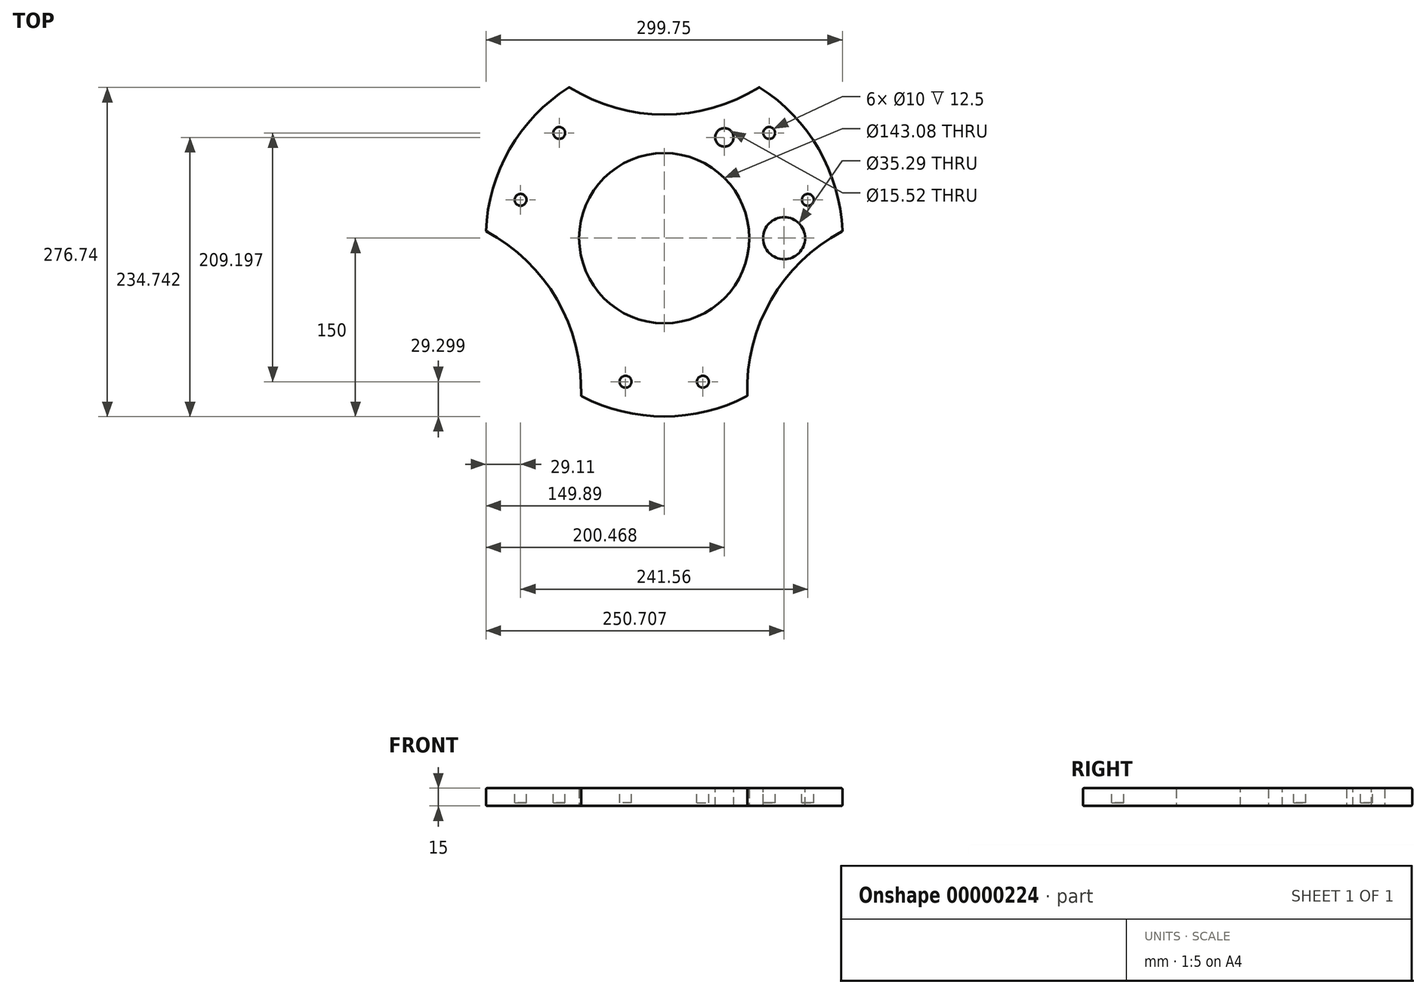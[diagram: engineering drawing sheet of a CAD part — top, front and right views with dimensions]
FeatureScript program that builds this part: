
annotation { "Feature Type Name" : "Feature", "Feature Type Description" : "" }
export const myFeature = defineFeature(function(context is Context, id is Id, definition is map)
    precondition{}
    {
        {
            var Q0;
            Q0 = qCreatedBy(makeId("Top.planeOp"), FACE);
            var sketch = newSketch(context, id + "F0", { "sketchPlane" : qUnion([Q0])});
            skLineSegment(sketch, "E0", {"start": v(0, 0) * mm, "end": v(0, -150) * mm, "construction": true});
            skArc(sketch, "E1", {"start": v(-61.95, 35.77) * mm, "mid": v(-61.95, -35.77) * mm, "end": v(0, -71.54) * mm});
            skArc(sketch, "E2", {"start": v(-129.9, 75) * mm, "mid": v(-144.12, 41.6) * mm, "end": v(-149.89, 5.76) * mm});
            skLineSegment(sketch, "E3", {"start": v(0, 0) * mm, "end": v(-129.9, -75) * mm, "construction": true});
            skArc(sketch, "E4", {"start": v(-69.95, -132.69) * mm, "mid": v(-89.94, -51.93) * mm, "end": v(-149.89, 5.76) * mm});
            skLineSegment(sketch, "E5", {"start": v(0, 0) * mm, "end": v(-129.9, 75) * mm, "construction": true});
            skLineSegment(sketch, "E6", {"start": v(-129.9, 75) * mm, "end": v(-61.95, 35.77) * mm});
            skLineSegment(sketch, "E7", {"start": v(0, -71.54) * mm, "end": v(0, -150) * mm});
            skArc(sketch, "E8.trimOffspring", {"start": v(-69.95, -132.69) * mm, "mid": v(-36.03, -145.6) * mm, "end": v(0, -150) * mm});
            skSolve(sketch);
        }
        {
            var Q0;
            Q0=makeQuery(id+"F0.imprint","IMPRINT",FACE,{"disambiguationData":[TD([[makeQuery(id+"F0.imprint","IMPRINT",EDGE,{"derivedFrom":sQuery(id+"F0.wireOp",EDGE,"E1")}),-1.0]])]});
            extrude(context, id + "F1", {"entities" : qUnion([Q0]), "depth" : 15 * mm});
        }
        {
            var Q0;
            Q0=makeQuery(id+"F1.opExtrude","CAP_FACE",FACE,{"disambiguationData":[OSD([sQuery(id+"F0.wireOp",EDGE,"E1"),sQuery(id+"F0.wireOp",EDGE,"E2"),sQuery(id+"F0.wireOp",EDGE,"E4"),sQuery(id+"F0.wireOp",EDGE,"E6"),sQuery(id+"F0.wireOp",EDGE,"E7"),sQuery(id+"F0.wireOp",EDGE,"E8.trimOffspring")])],"isStart":false});
            var sketch = newSketch(context, id + "F2", { "sketchPlane" : qUnion([Q0])});
            skCircle(sketch, "E9", {"center": v(-32.5, -120.7) * mm, "radius": 5 * mm});
            skCircle(sketch, "E10", {"center": v(0, 0) * mm, "radius": 125 * mm, "construction": true});
            skLineSegment(sketch, "E11.0", {"start": v(0, 0) * mm, "end": v(-129.9, -75) * mm, "construction": true});
            skLineSegment(sketch, "E12.0", {"start": v(0, 0) * mm, "end": v(0, -150) * mm, "construction": true});
            skSolve(sketch);
        }
        {
            var Q0;
            Q0=makeQuery(id+"F2.imprint","IMPRINT",FACE,{"disambiguationData":[TD([[makeQuery(id+"F2.imprint","IMPRINT",EDGE,{"derivedFrom":sQuery(id+"F2.wireOp",EDGE,"E9")}),1.0]])]});
            extrude(context, id + "F3", {"entities" : qUnion([Q0]), "oppositeDirection" : true, "depth" : 12.5 * mm});
        }
        {
            var Q0;
            Q0=sQuery(id+"F0.wireOp",EDGE,"E3");
            cPlane(context, id + "F4", {"entities" : qUnion([Q0]), "cplaneType" : CPlaneType.LINE_ANGLE, "offset" : 150 * mm, "angle" : 0 * degree, "width" : 150 * mm, "height" : 150 * mm});
        }
        {
            var Q0;
            Q0=makeQuery(id+"F3.opExtrude","SWEPT_BODY",BODY,{"disambiguationData":[OSD([sQuery(id+"F2.wireOp",EDGE,"E9")])]});
            var Q1;
            Q1=qCreatedBy(id+"F4.planeOp",FACE);
            mirror(context, id + "F5", {"entities" : qUnion([Q0]), "mirrorPlane" : qUnion([Q1])});
        }
        {
            var Q0;
            Q0=makeQuery(id+"F3.opExtrude","SWEPT_BODY",BODY,{"disambiguationData":[OSD([sQuery(id+"F2.wireOp",EDGE,"E9")])]});
            var Q1;
            Q1=makeQuery(id+"F5.opPattern","COPY",BODY,{"derivedFrom":makeQuery(id+"F3.opExtrude","SWEPT_BODY",BODY,{"disambiguationData":[OSD([sQuery(id+"F2.wireOp",EDGE,"E9")])]}),"instanceName":"1"});
            var Q2;
            Q2=makeQuery(id+"F1.opExtrude","SWEPT_BODY",BODY,{"disambiguationData":[OSD([sQuery(id+"F0.wireOp",EDGE,"E1"),sQuery(id+"F0.wireOp",EDGE,"E2"),sQuery(id+"F0.wireOp",EDGE,"E4"),sQuery(id+"F0.wireOp",EDGE,"E6"),sQuery(id+"F0.wireOp",EDGE,"E7"),sQuery(id+"F0.wireOp",EDGE,"E8.trimOffspring")])]});
            booleanBodies(context, id + "F6", {"operationType" : BooleanOperationType.SUBTRACTION, "tools" : qUnion([Q0, Q1]), "targets" : qUnion([Q2])});
        }
        {
            var Q0;
            Q0=makeQuery(id+"F1.opExtrude","SWEPT_BODY",BODY,{"disambiguationData":[OSD([sQuery(id+"F0.wireOp",EDGE,"E1"),sQuery(id+"F0.wireOp",EDGE,"E2"),sQuery(id+"F0.wireOp",EDGE,"E4"),sQuery(id+"F0.wireOp",EDGE,"E6"),sQuery(id+"F0.wireOp",EDGE,"E7"),sQuery(id+"F0.wireOp",EDGE,"E8.trimOffspring")])]});
            var Q1;
            Q1=makeQuery(id+"F1.opExtrude","SWEPT_FACE",FACE,{"disambiguationData":[OSD([sQuery(id+"F0.wireOp",EDGE,"E1")])]});
            circularPattern(context, id + "F7", {"entities" : qUnion([Q0]), "axis" : qUnion([Q1]), "angle" : 360 * degree, "instanceCount" : 3, "equalSpace" : true});
        }
        {
            var Q0;
            Q0=makeQuery(id+"F1.opExtrude","SWEPT_BODY",BODY,{"disambiguationData":[OSD([sQuery(id+"F0.wireOp",EDGE,"E1"),sQuery(id+"F0.wireOp",EDGE,"E2"),sQuery(id+"F0.wireOp",EDGE,"E4"),sQuery(id+"F0.wireOp",EDGE,"E6"),sQuery(id+"F0.wireOp",EDGE,"E7"),sQuery(id+"F0.wireOp",EDGE,"E8.trimOffspring")])]});
            var Q1;
            Q1=makeQuery(id+"F7.opPattern","COPY",BODY,{"derivedFrom":makeQuery(id+"F1.opExtrude","SWEPT_BODY",BODY,{"disambiguationData":[OSD([sQuery(id+"F0.wireOp",EDGE,"E1"),sQuery(id+"F0.wireOp",EDGE,"E2"),sQuery(id+"F0.wireOp",EDGE,"E4"),sQuery(id+"F0.wireOp",EDGE,"E6"),sQuery(id+"F0.wireOp",EDGE,"E7"),sQuery(id+"F0.wireOp",EDGE,"E8.trimOffspring")])]}),"instanceName":"2"});
            var Q2;
            Q2=makeQuery(id+"F7.opPattern","COPY",BODY,{"derivedFrom":makeQuery(id+"F1.opExtrude","SWEPT_BODY",BODY,{"disambiguationData":[OSD([sQuery(id+"F0.wireOp",EDGE,"E1"),sQuery(id+"F0.wireOp",EDGE,"E2"),sQuery(id+"F0.wireOp",EDGE,"E4"),sQuery(id+"F0.wireOp",EDGE,"E6"),sQuery(id+"F0.wireOp",EDGE,"E7"),sQuery(id+"F0.wireOp",EDGE,"E8.trimOffspring")])]}),"instanceName":"1"});
            booleanBodies(context, id + "F8", {"operationType" : BooleanOperationType.UNION, "tools" : qUnion([Q0, Q1, Q2])});
        }
        {
            var Q0;
            Q0=makeQuery(id+"F8.opBoolean","MERGE",EDGE,{"derivedFrom":[makeQuery(id+"F1.opExtrude","CAP_EDGE",EDGE,{"disambiguationData":[OSD([sQuery(id+"F0.wireOp",EDGE,"E8.trimOffspring")])],"isStart":false}),makeQuery(id+"F7.opPattern","COPY",EDGE,{"derivedFrom":makeQuery(id+"F1.opExtrude","CAP_EDGE",EDGE,{"disambiguationData":[OSD([sQuery(id+"F0.wireOp",EDGE,"E2")])],"isStart":false}),"instanceName":"1"})]});
            var Q1;
            Q1=makeQuery(id+"F7.opPattern","COPY",EDGE,{"derivedFrom":makeQuery(id+"F1.opExtrude","SWEPT_EDGE",EDGE,{"disambiguationData":[OSD([sQuery(id+"F0.wireOp",EDGE,"E2"),sQuery(id+"F0.wireOp",EDGE,"E4")])]}),"instanceName":"1"});
            var Q2;
            Q2=makeQuery(id+"F7.opPattern","COPY",EDGE,{"derivedFrom":makeQuery(id+"F1.opExtrude","CAP_EDGE",EDGE,{"disambiguationData":[OSD([sQuery(id+"F0.wireOp",EDGE,"E4")])],"isStart":false}),"instanceName":"1"});
            var Q3;
            Q3=makeQuery(id+"F7.opPattern","COPY",EDGE,{"derivedFrom":makeQuery(id+"F1.opExtrude","SWEPT_EDGE",EDGE,{"disambiguationData":[OSD([sQuery(id+"F0.wireOp",EDGE,"E4"),sQuery(id+"F0.wireOp",EDGE,"E8.trimOffspring")])]}),"instanceName":"1"});
            var Q4;
            Q4=makeQuery(id+"F8.opBoolean","MERGE",EDGE,{"derivedFrom":[makeQuery(id+"F7.opPattern","COPY",EDGE,{"derivedFrom":makeQuery(id+"F1.opExtrude","CAP_EDGE",EDGE,{"disambiguationData":[OSD([sQuery(id+"F0.wireOp",EDGE,"E8.trimOffspring")])],"isStart":false}),"instanceName":"1"}),makeQuery(id+"F7.opPattern","COPY",EDGE,{"derivedFrom":makeQuery(id+"F1.opExtrude","CAP_EDGE",EDGE,{"disambiguationData":[OSD([sQuery(id+"F0.wireOp",EDGE,"E2")])],"isStart":false}),"instanceName":"2"})]});
            var Q5;
            Q5=makeQuery(id+"F7.opPattern","COPY",EDGE,{"derivedFrom":makeQuery(id+"F1.opExtrude","SWEPT_EDGE",EDGE,{"disambiguationData":[OSD([sQuery(id+"F0.wireOp",EDGE,"E2"),sQuery(id+"F0.wireOp",EDGE,"E4")])]}),"instanceName":"2"});
            var Q6;
            Q6=makeQuery(id+"F7.opPattern","COPY",EDGE,{"derivedFrom":makeQuery(id+"F1.opExtrude","CAP_EDGE",EDGE,{"disambiguationData":[OSD([sQuery(id+"F0.wireOp",EDGE,"E4")])],"isStart":false}),"instanceName":"2"});
            var Q7;
            Q7=makeQuery(id+"F7.opPattern","COPY",EDGE,{"derivedFrom":makeQuery(id+"F1.opExtrude","SWEPT_EDGE",EDGE,{"disambiguationData":[OSD([sQuery(id+"F0.wireOp",EDGE,"E4"),sQuery(id+"F0.wireOp",EDGE,"E8.trimOffspring")])]}),"instanceName":"2"});
            var Q8;
            Q8=makeQuery(id+"F8.opBoolean","MERGE",EDGE,{"derivedFrom":[makeQuery(id+"F1.opExtrude","CAP_EDGE",EDGE,{"disambiguationData":[OSD([sQuery(id+"F0.wireOp",EDGE,"E2")])],"isStart":false}),makeQuery(id+"F7.opPattern","COPY",EDGE,{"derivedFrom":makeQuery(id+"F1.opExtrude","CAP_EDGE",EDGE,{"disambiguationData":[OSD([sQuery(id+"F0.wireOp",EDGE,"E8.trimOffspring")])],"isStart":false}),"instanceName":"2"})]});
            var Q9;
            Q9=makeQuery(id+"F1.opExtrude","CAP_EDGE",EDGE,{"disambiguationData":[OSD([sQuery(id+"F0.wireOp",EDGE,"E4")])],"isStart":false});
            var Q10;
            Q10=makeQuery(id+"F1.opExtrude","SWEPT_EDGE",EDGE,{"disambiguationData":[OSD([sQuery(id+"F0.wireOp",EDGE,"E4"),sQuery(id+"F0.wireOp",EDGE,"E8.trimOffspring")])]});
            var Q11;
            Q11=makeQuery(id+"F8.opBoolean","MERGE",EDGE,{"derivedFrom":[makeQuery(id+"F1.opExtrude","CAP_EDGE",EDGE,{"disambiguationData":[OSD([sQuery(id+"F0.wireOp",EDGE,"E8.trimOffspring")])],"isStart":true}),makeQuery(id+"F7.opPattern","COPY",EDGE,{"derivedFrom":makeQuery(id+"F1.opExtrude","CAP_EDGE",EDGE,{"disambiguationData":[OSD([sQuery(id+"F0.wireOp",EDGE,"E2")])],"isStart":true}),"instanceName":"1"})]});
            var Q12;
            Q12=makeQuery(id+"F1.opExtrude","CAP_EDGE",EDGE,{"disambiguationData":[OSD([sQuery(id+"F0.wireOp",EDGE,"E4")])],"isStart":true});
            var Q13;
            Q13=makeQuery(id+"F7.opPattern","COPY",EDGE,{"derivedFrom":makeQuery(id+"F1.opExtrude","CAP_EDGE",EDGE,{"disambiguationData":[OSD([sQuery(id+"F0.wireOp",EDGE,"E4")])],"isStart":true}),"instanceName":"1"});
            var Q14;
            Q14=makeQuery(id+"F8.opBoolean","MERGE",EDGE,{"derivedFrom":[makeQuery(id+"F7.opPattern","COPY",EDGE,{"derivedFrom":makeQuery(id+"F1.opExtrude","CAP_EDGE",EDGE,{"disambiguationData":[OSD([sQuery(id+"F0.wireOp",EDGE,"E8.trimOffspring")])],"isStart":true}),"instanceName":"1"}),makeQuery(id+"F7.opPattern","COPY",EDGE,{"derivedFrom":makeQuery(id+"F1.opExtrude","CAP_EDGE",EDGE,{"disambiguationData":[OSD([sQuery(id+"F0.wireOp",EDGE,"E2")])],"isStart":true}),"instanceName":"2"})]});
            var Q15;
            Q15=makeQuery(id+"F7.opPattern","COPY",EDGE,{"derivedFrom":makeQuery(id+"F1.opExtrude","CAP_EDGE",EDGE,{"disambiguationData":[OSD([sQuery(id+"F0.wireOp",EDGE,"E4")])],"isStart":true}),"instanceName":"2"});
            var Q16;
            Q16=makeQuery(id+"F8.opBoolean","MERGE",EDGE,{"derivedFrom":[makeQuery(id+"F1.opExtrude","CAP_EDGE",EDGE,{"disambiguationData":[OSD([sQuery(id+"F0.wireOp",EDGE,"E2")])],"isStart":true}),makeQuery(id+"F7.opPattern","COPY",EDGE,{"derivedFrom":makeQuery(id+"F1.opExtrude","CAP_EDGE",EDGE,{"disambiguationData":[OSD([sQuery(id+"F0.wireOp",EDGE,"E8.trimOffspring")])],"isStart":true}),"instanceName":"2"})]});
            var Q17;
            {var subQ0=makeQuery(id+"F1.opExtrude","CAP_EDGE",EDGE,{"disambiguationData":[OSD([sQuery(id+"F0.wireOp",EDGE,"E1")])],"isStart":true});Q17=makeQuery(id+"F8.opBoolean","MERGE",EDGE,{"derivedFrom":[subQ0,makeQuery(id+"F7.opPattern","COPY",EDGE,{"derivedFrom":subQ0,"instanceName":"1"}),makeQuery(id+"F7.opPattern","COPY",EDGE,{"derivedFrom":subQ0,"instanceName":"2"})]});}
            var Q18;
            {var subQ0=makeQuery(id+"F1.opExtrude","CAP_EDGE",EDGE,{"disambiguationData":[OSD([sQuery(id+"F0.wireOp",EDGE,"E1")])],"isStart":false});Q18=makeQuery(id+"F8.opBoolean","MERGE",EDGE,{"derivedFrom":[subQ0,makeQuery(id+"F7.opPattern","COPY",EDGE,{"derivedFrom":subQ0,"instanceName":"1"}),makeQuery(id+"F7.opPattern","COPY",EDGE,{"derivedFrom":subQ0,"instanceName":"2"})]});}
            fillet(context, id + "F9", {"entities" : qUnion([Q0, Q1, Q2, Q3, Q4, Q5, Q6, Q7, Q8, Q9, Q10, Q11, Q12, Q13, Q14, Q15, Q16, Q17, Q18]), "radius" : 1 * mm, "tangentPropagation" : true, "allowEdgeOverflow" : false});
        }
        {
            var Q0;
            {var subQ0=makeQuery(id+"F1.opExtrude","CAP_FACE",FACE,{"disambiguationData":[OSD([sQuery(id+"F0.wireOp",EDGE,"E1"),sQuery(id+"F0.wireOp",EDGE,"E2"),sQuery(id+"F0.wireOp",EDGE,"E4"),sQuery(id+"F0.wireOp",EDGE,"E6"),sQuery(id+"F0.wireOp",EDGE,"E7"),sQuery(id+"F0.wireOp",EDGE,"E8.trimOffspring")])],"isStart":false});Q0=makeQuery(id+"F8.opBoolean","MERGE",FACE,{"derivedFrom":[subQ0,makeQuery(id+"F7.opPattern","COPY",FACE,{"derivedFrom":subQ0,"instanceName":"1"}),makeQuery(id+"F7.opPattern","COPY",FACE,{"derivedFrom":subQ0,"instanceName":"2"})]});}
            var sketch = newSketch(context, id + "F10", { "sketchPlane" : qUnion([Q0])});
            skCircle(sketch, "E13", {"center": v(100.82, 0) * mm, "radius": 17.65 * mm});
            skSolve(sketch);
        }
        {
            var Q0;
            Q0=makeQuery(id+"F10.imprint","IMPRINT",FACE,{"disambiguationData":[TD([[makeQuery(id+"F10.imprint","IMPRINT",EDGE,{"derivedFrom":sQuery(id+"F10.wireOp",EDGE,"E13")}),1.0]])]});
            extrude(context, id + "F11", {"entities" : qUnion([Q0]), "operationType" : NewBodyOperationType.REMOVE, "oppositeDirection" : true, "depth" : 103.48 * mm});
        }
        {
            var Q0;
            {var subQ0=makeQuery(id+"F1.opExtrude","CAP_FACE",FACE,{"disambiguationData":[OSD([sQuery(id+"F0.wireOp",EDGE,"E1"),sQuery(id+"F0.wireOp",EDGE,"E2"),sQuery(id+"F0.wireOp",EDGE,"E4"),sQuery(id+"F0.wireOp",EDGE,"E6"),sQuery(id+"F0.wireOp",EDGE,"E7"),sQuery(id+"F0.wireOp",EDGE,"E8.trimOffspring")])],"isStart":false});Q0=makeQuery(id+"F8.opBoolean","MERGE",FACE,{"derivedFrom":[subQ0,makeQuery(id+"F7.opPattern","COPY",FACE,{"derivedFrom":subQ0,"instanceName":"1"}),makeQuery(id+"F7.opPattern","COPY",FACE,{"derivedFrom":subQ0,"instanceName":"2"})]});}
            var sketch = newSketch(context, id + "F12", { "sketchPlane" : qUnion([Q0])});
            skCircle(sketch, "E14", {"center": v(50.58, 84.74) * mm, "radius": 7.76 * mm});
            skSolve(sketch);
        }
        {
            var Q0;
            Q0=makeQuery(id+"F12.imprint","IMPRINT",FACE,{"disambiguationData":[TD([[makeQuery(id+"F12.imprint","IMPRINT",EDGE,{"derivedFrom":sQuery(id+"F12.wireOp",EDGE,"E14")}),1.0]])]});
            extrude(context, id + "F13", {"entities" : qUnion([Q0]), "operationType" : NewBodyOperationType.REMOVE, "oppositeDirection" : true, "depth" : 25.4 * mm});
        }
    });
